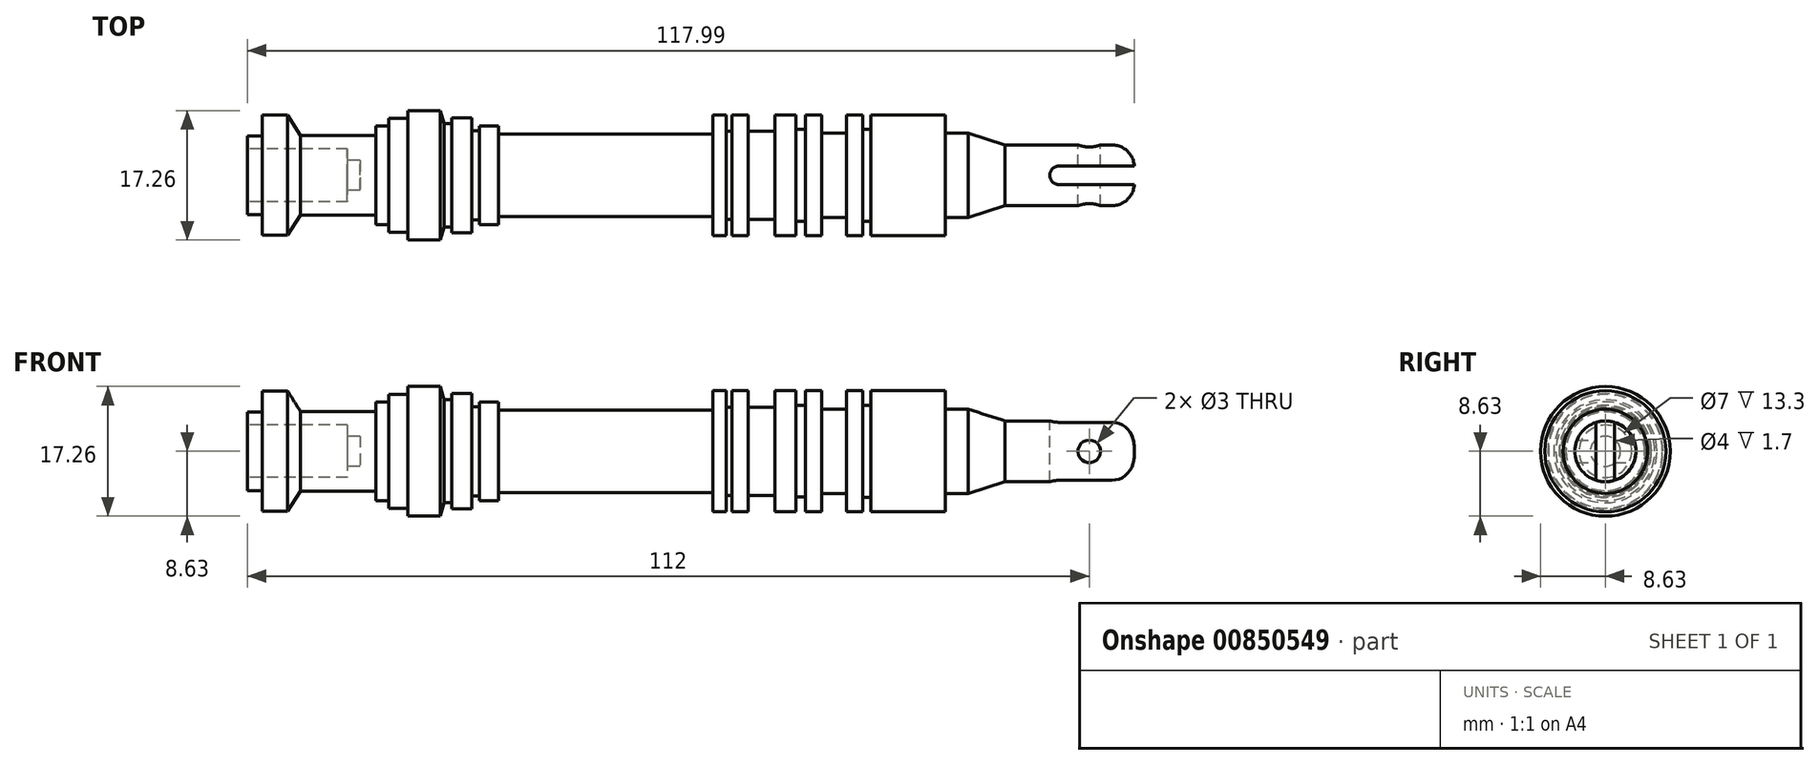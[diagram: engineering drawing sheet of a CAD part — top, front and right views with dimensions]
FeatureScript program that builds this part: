
annotation { "Feature Type Name" : "Feature", "Feature Type Description" : "" }
export const myFeature = defineFeature(function(context is Context, id is Id, definition is map)
    precondition{}
    {
        {
            var Q0;
            Q0=qCreatedBy(makeId("Front.planeOp"),FACE);
            var sketch = newSketch(context, id + "F0", { "sketchPlane" : qUnion([Q0])});
            skLineSegment(sketch, "E0", {"start": v(0, 0) * mm, "end": v(118, 0) * mm, "construction": true});
            skLineSegment(sketch, "E1", {"start": v(0, 3.5) * mm, "end": v(13.3, 3.5) * mm});
            skLineSegment(sketch, "E2", {"start": v(13.3, 3.5) * mm, "end": v(13.3, 2) * mm});
            skLineSegment(sketch, "E3", {"start": v(13.3, 2) * mm, "end": v(15, 2) * mm});
            skLineSegment(sketch, "E4", {"start": v(15, 2) * mm, "end": v(15, 0) * mm});
            skLineSegment(sketch, "E5", {"start": v(0, 3.5) * mm, "end": v(0, 5.23) * mm});
            skLineSegment(sketch, "E6", {"start": v(0, 5.23) * mm, "end": v(1.99, 5.23) * mm});
            skLineSegment(sketch, "E7", {"start": v(1.99, 5.23) * mm, "end": v(1.99, 8) * mm});
            skLineSegment(sketch, "E8", {"start": v(1.99, 8) * mm, "end": v(5.38, 8) * mm});
            skLineSegment(sketch, "E9", {"start": v(5.38, 8) * mm, "end": v(7.07, 5.3) * mm});
            skLineSegment(sketch, "E10", {"start": v(7.07, 5.3) * mm, "end": v(17.07, 5.3) * mm});
            skLineSegment(sketch, "E11", {"start": v(17.07, 5.3) * mm, "end": v(17.07, 6.58) * mm});
            skLineSegment(sketch, "E12", {"start": v(17.07, 6.58) * mm, "end": v(18.83, 6.58) * mm});
            skLineSegment(sketch, "E13", {"start": v(18.83, 6.58) * mm, "end": v(18.83, 7.58) * mm});
            skLineSegment(sketch, "E14", {"start": v(18.83, 7.58) * mm, "end": v(21.34, 7.58) * mm});
            skLineSegment(sketch, "E15", {"start": v(21.34, 7.58) * mm, "end": v(21.34, 8.63) * mm});
            skLineSegment(sketch, "E16", {"start": v(21.34, 8.63) * mm, "end": v(25.68, 8.63) * mm});
            skLineSegment(sketch, "E17", {"start": v(25.68, 8.63) * mm, "end": v(26.19, 6.86) * mm});
            skLineSegment(sketch, "E18", {"start": v(26.19, 6.86) * mm, "end": v(27.2, 6.86) * mm});
            skLineSegment(sketch, "E19", {"start": v(27.2, 6.86) * mm, "end": v(27.2, 7.68) * mm});
            skLineSegment(sketch, "E20", {"start": v(27.2, 7.68) * mm, "end": v(29.83, 7.68) * mm});
            skLineSegment(sketch, "E21", {"start": v(29.83, 7.68) * mm, "end": v(29.83, 5.93) * mm});
            skLineSegment(sketch, "E22", {"start": v(29.83, 5.93) * mm, "end": v(30.85, 5.93) * mm});
            skLineSegment(sketch, "E23", {"start": v(30.85, 5.93) * mm, "end": v(30.85, 6.58) * mm});
            skLineSegment(sketch, "E24", {"start": v(30.85, 6.58) * mm, "end": v(33.42, 6.58) * mm});
            skLineSegment(sketch, "E25", {"start": v(33.42, 6.58) * mm, "end": v(33.42, 5.5) * mm});
            skLineSegment(sketch, "E26", {"start": v(33.42, 5.5) * mm, "end": v(61.92, 5.5) * mm});
            skLineSegment(sketch, "E27", {"start": v(61.92, 5.5) * mm, "end": v(61.92, 8.06) * mm});
            skLineSegment(sketch, "E28", {"start": v(61.92, 8.06) * mm, "end": v(63.67, 8.06) * mm});
            skLineSegment(sketch, "E29", {"start": v(63.67, 8.06) * mm, "end": v(63.67, 5.86) * mm});
            skLineSegment(sketch, "E30", {"start": v(63.67, 5.86) * mm, "end": v(64.5, 5.86) * mm});
            skLineSegment(sketch, "E31", {"start": v(64.5, 5.86) * mm, "end": v(64.5, 8.06) * mm});
            skLineSegment(sketch, "E32", {"start": v(64.5, 8.06) * mm, "end": v(66.63, 8.06) * mm});
            skLineSegment(sketch, "E33", {"start": v(66.63, 8.06) * mm, "end": v(66.63, 5.87) * mm});
            skLineSegment(sketch, "E34", {"start": v(66.63, 5.87) * mm, "end": v(70.15, 5.87) * mm});
            skLineSegment(sketch, "E35", {"start": v(70.15, 5.87) * mm, "end": v(70.15, 8.06) * mm});
            skLineSegment(sketch, "E36", {"start": v(70.15, 8.06) * mm, "end": v(72.94, 8.06) * mm});
            skLineSegment(sketch, "E37", {"start": v(72.94, 8.06) * mm, "end": v(72.94, 6.1) * mm});
            skLineSegment(sketch, "E38", {"start": v(72.94, 6.1) * mm, "end": v(74.23, 6.1) * mm});
            skLineSegment(sketch, "E39", {"start": v(74.23, 6.1) * mm, "end": v(74.23, 8.06) * mm});
            skLineSegment(sketch, "E40", {"start": v(74.23, 8.06) * mm, "end": v(76.37, 8.06) * mm});
            skLineSegment(sketch, "E41", {"start": v(76.37, 8.06) * mm, "end": v(76.37, 5.61) * mm});
            skLineSegment(sketch, "E42", {"start": v(76.37, 5.61) * mm, "end": v(79.73, 5.61) * mm});
            skLineSegment(sketch, "E43", {"start": v(79.73, 5.61) * mm, "end": v(79.73, 8.06) * mm});
            skLineSegment(sketch, "E44", {"start": v(79.73, 8.06) * mm, "end": v(81.86, 8.06) * mm});
            skLineSegment(sketch, "E45", {"start": v(81.86, 8.06) * mm, "end": v(81.86, 6.15) * mm});
            skLineSegment(sketch, "E46", {"start": v(81.86, 6.15) * mm, "end": v(82.92, 6.15) * mm});
            skLineSegment(sketch, "E47", {"start": v(82.92, 6.15) * mm, "end": v(82.92, 8.06) * mm});
            skLineSegment(sketch, "E48", {"start": v(82.92, 8.06) * mm, "end": v(92.82, 8.06) * mm});
            skLineSegment(sketch, "E49", {"start": v(92.82, 8.06) * mm, "end": v(92.82, 5.61) * mm});
            skLineSegment(sketch, "E50", {"start": v(92.82, 5.61) * mm, "end": v(95.9, 5.61) * mm});
            skLineSegment(sketch, "E51", {"start": v(95.9, 5.61) * mm, "end": v(100.77, 4.06) * mm});
            skLineSegment(sketch, "E52", {"start": v(100.77, 4.06) * mm, "end": v(115, 4.06) * mm});
            skLineSegment(sketch, "E53", {"start": v(118, 1.06) * mm, "end": v(118, 0) * mm});
            skPoint(sketch, "E54.visualSharp", {"position": v(118, 4.06) * mm});
            skArc(sketch, "E54.filletArc", {"start": v(118, 1.06) * mm, "mid": v(117.12, 3.18) * mm, "end": v(115, 4.06) * mm});
            skLineSegment(sketch, "E55", {"start": v(15, 0) * mm, "end": v(118, 0) * mm});
            skSolve(sketch);
        }
        {
            var Q0;
            Q0=makeQuery(id+"F0.imprint","IMPRINT",FACE,{"disambiguationData":[TD([[makeQuery(id+"F0.imprint","IMPRINT",EDGE,{"derivedFrom":sQuery(id+"F0.wireOp",EDGE,"E1")}),1.0]])]});
            var Q1;
            Q1=sQuery(id+"F0.wireOp",EDGE,"E55");
            revolve(context, id + "F1", {"surfaceOperationType" : NewSurfaceOperationType.NEW, "entities" : qUnion([Q0]), "axis" : qUnion([Q1]), "revolveType" : RevolveType.FULL});
        }
        {
            var Q0;
            Q0=qCreatedBy(makeId("Front.planeOp"),FACE);
            var sketch = newSketch(context, id + "F2", { "sketchPlane" : qUnion([Q0])});
            skCircle(sketch, "E56", {"center": v(112, 0) * mm, "radius": 1.5 * mm});
            skSolve(sketch);
        }
        {
            var Q0;
            Q0 = qSketchRegion(id + "F2", true);
            extrude(context, id + "F3", {"entities" : qUnion([Q0]), "operationType" : NewBodyOperationType.REMOVE, "endBound" : BoundingType.SYMMETRIC, "depth" : 25.4 * mm, "offsetDistance" : 25.4 * mm});
        }
        {
            var Q0;
            Q0=qCreatedBy(makeId("Top.planeOp"),FACE);
            var sketch = newSketch(context, id + "F4", { "sketchPlane" : qUnion([Q0])});
            skArc(sketch, "E57", {"start": v(108, 1.25) * mm, "mid": v(106.75, 0) * mm, "end": v(108, -1.25) * mm});
            skLineSegment(sketch, "E58", {"start": v(108, 1.25) * mm, "end": v(119.2, 1.25) * mm});
            skLineSegment(sketch, "E59", {"start": v(119.2, 1.25) * mm, "end": v(119.2, -1.25) * mm});
            skLineSegment(sketch, "E60", {"start": v(119.2, -1.25) * mm, "end": v(108, -1.25) * mm});
            skSolve(sketch);
        }
        {
            var Q0;
            Q0 = qSketchRegion(id + "F4", true);
            extrude(context, id + "F5", {"entities" : qUnion([Q0]), "operationType" : NewBodyOperationType.REMOVE, "endBound" : BoundingType.SYMMETRIC, "oppositeDirection" : true, "depth" : 25 * mm, "offsetDistance" : 25 * mm});
        }
    });
